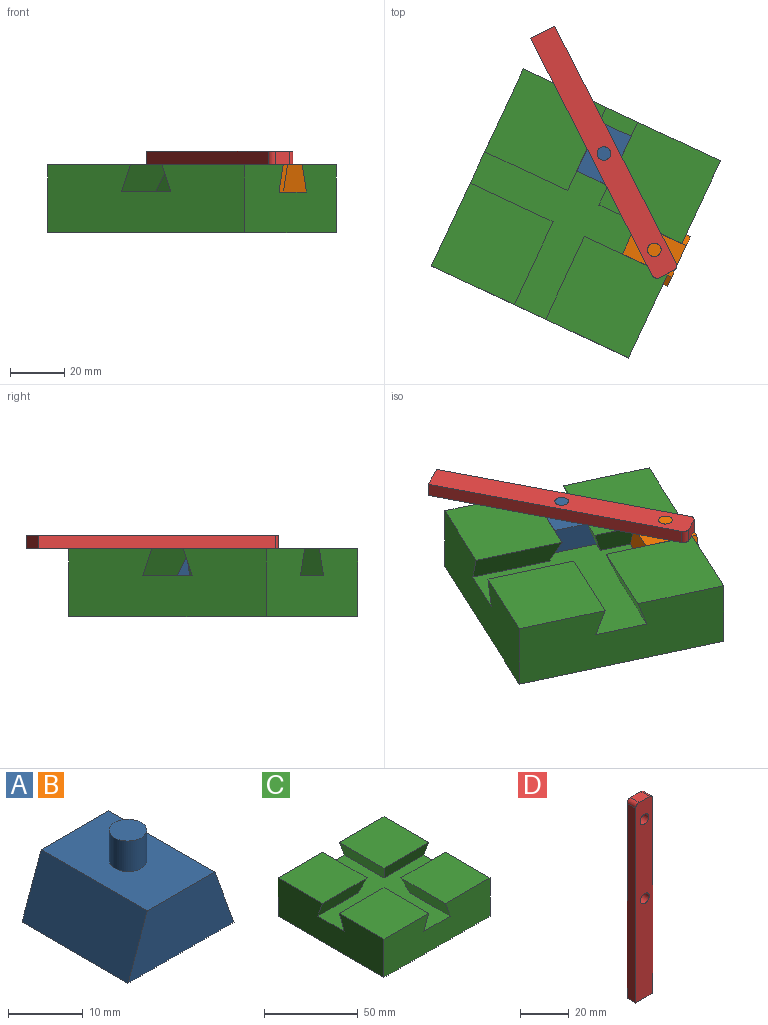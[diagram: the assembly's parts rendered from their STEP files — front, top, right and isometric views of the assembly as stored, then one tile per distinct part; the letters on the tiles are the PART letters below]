
ASSEMBLY  parts=4 mates=4
PART A: 8 faces, bbox 20x20x15 mm
  f0: plane 20x12.72mm, normal (0,0,1), area 234.8mm2, adj f1,f3,f4,f5,f6
  f1: plane 20x10mm, normal (-0.94,0,0.34), area 212.8mm2, adj f0,f2,f4,f5
  f2: plane 20x20mm, normal (0,0,-1), area 400mm2, adj f1,f3,f4,f5
  f3: plane 20x10mm, normal (0.94,0,0.34), area 212.8mm2, adj f0,f2,f4,f5
  f4: plane 20x10mm, normal (0,-1,0), area 163.6mm2, adj f0,f1,f2,f3
  f5: plane 20x10mm, normal (0,1,0), area 163.6mm2, adj f0,f1,f2,f3
  f6: cylinder r=2.5mm len=5mm, axis (0,0,-1), area 78.5mm2, adj f0,f7
  f7: plane 5x5mm, normal (0,0,1), area 19.6mm2, adj f6
PART B: same geometry as A
PART C: 18 faces, bbox 80x80x25 mm
  f0: plane 33.64x33.64mm, normal (0,0,1), area 1131.6mm2, adj f2,f7,f12,f17
  f1: plane 33.64x33.64mm, normal (0,0,1), area 1131.6mm2, adj f3,f4,f12,f15
  f2: plane 33.64x10mm, normal (0.94,0,-0.34), area 338.6mm2, adj f0,f11,f12,f17
  f3: plane 80x25mm, normal (1,0,0), area 1836.4mm2, adj f1,f8,f9,f11,f12,f13,f14,f15
  f4: plane 33.64x10mm, normal (-0.94,0,-0.34), area 338.6mm2, adj f1,f11,f12,f15
  f5: plane 33.64x10mm, normal (0.94,0,-0.34), area 338.6mm2, adj f6,f11,f13,f16
  f6: plane 33.64x33.64mm, normal (0,0,1), area 1131.6mm2, adj f5,f7,f13,f16
  f7: plane 80x25mm, normal (-1,0,0), area 1836.4mm2, adj f0,f6,f8,f11,f12,f13,f16,f17
  f8: plane 80x80mm, normal (0,0,-1), area 6400mm2, adj f3,f7,f12,f13
  f9: plane 33.64x33.64mm, normal (0,0,1), area 1131.6mm2, adj f3,f10,f13,f14
  f10: plane 33.64x10mm, normal (-0.94,0,-0.34), area 338.6mm2, adj f9,f11,f13,f14
  f11: plane 80x80mm, normal (0,0,1), area 2800mm2, adj f2,f3,f4,f5,f7,f10,f12,f13
  f12: plane 80x25mm, normal (0,-1,0), area 1836.4mm2, adj f0,f1,f2,f3,f4,f7,f8,f11
  f13: plane 80x25mm, normal (0,1,0), area 1836.4mm2, adj f3,f5,f6,f7,f8,f9,f10,f11
  f14: plane 33.64x10mm, normal (0,-0.94,-0.34), area 338.6mm2, adj f3,f9,f10,f11
  f15: plane 33.64x10mm, normal (0,0.94,-0.34), area 338.6mm2, adj f1,f3,f4,f11
  f16: plane 33.64x10mm, normal (0,-0.94,-0.34), area 338.6mm2, adj f5,f6,f7,f11
  f17: plane 33.64x10mm, normal (0,0.94,-0.34), area 338.6mm2, adj f0,f2,f7,f11
PART D: 10 faces, bbox 10x5x100 mm
  f0: plane 6x5mm, normal (0,0,1), area 30mm2, adj f1,f7,f8,f9
  f1: cylinder r=2mm len=5mm, axis (0,1,0), area 15.7mm2, adj f0,f2,f8,f9
  f2: plane 98x5mm, normal (-1,0,0), area 490mm2, adj f1,f3,f8,f9
  f3: plane 10x5mm, normal (0,0,-1), area 50mm2, adj f2,f4,f8,f9
  f4: plane 98x5mm, normal (1,0,0), area 490mm2, adj f3,f7,f8,f9
  f5: cylinder r=2.5mm len=5mm, axis (0,1,0), area 78.5mm2, adj f8,f9
  f6: cylinder r=2.5mm len=5mm, axis (0,1,0), area 78.5mm2, adj f8,f9
  f7: cylinder r=2mm len=5mm, axis (0,1,0), area 15.7mm2, adj f0,f4,f8,f9
  f8: plane 100x10mm, normal (0,-1,0), area 959mm2, adj f0,f1,f2,f3,f4,f5,f6,f7
  f9: plane 100x10mm, normal (0,1,0), area 959mm2, adj f0,f1,f2,f3,f4,f5,f6,f7
PLACE A rot(axis=(0,0,-1),25deg) t=(-154.06,-204.13,-8.16)mm
PLACE B rot(axis=(0,0,1),65deg) t=(-153.65,-231.13,-8.16)mm
PLACE C rot(axis=(0,0,-1),25deg) t=(-124.46,-211.64,-23.16)mm
PLACE D rot(axis=(-0.17,0.7,-0.7),160.9deg) t=(-194.33,-166.62,1.84)mm
MATE slider A.f4 <-> C.f12  axis (-0.42,-0.91,0) through (-171.57,-218.03,-8.16)mm
MATE slider B.f5 <-> C.f7  axis (-0.91,0.42,0) through (-157.87,-240.19,-8.16)mm
MATE revolute A.f6 <-> D.f5  axis (0,0,1) through (-167.34,-208.97,6.84)mm
MATE revolute B.f6 <-> D.f6  axis (0,0,1) through (-148.81,-244.42,6.84)mm
